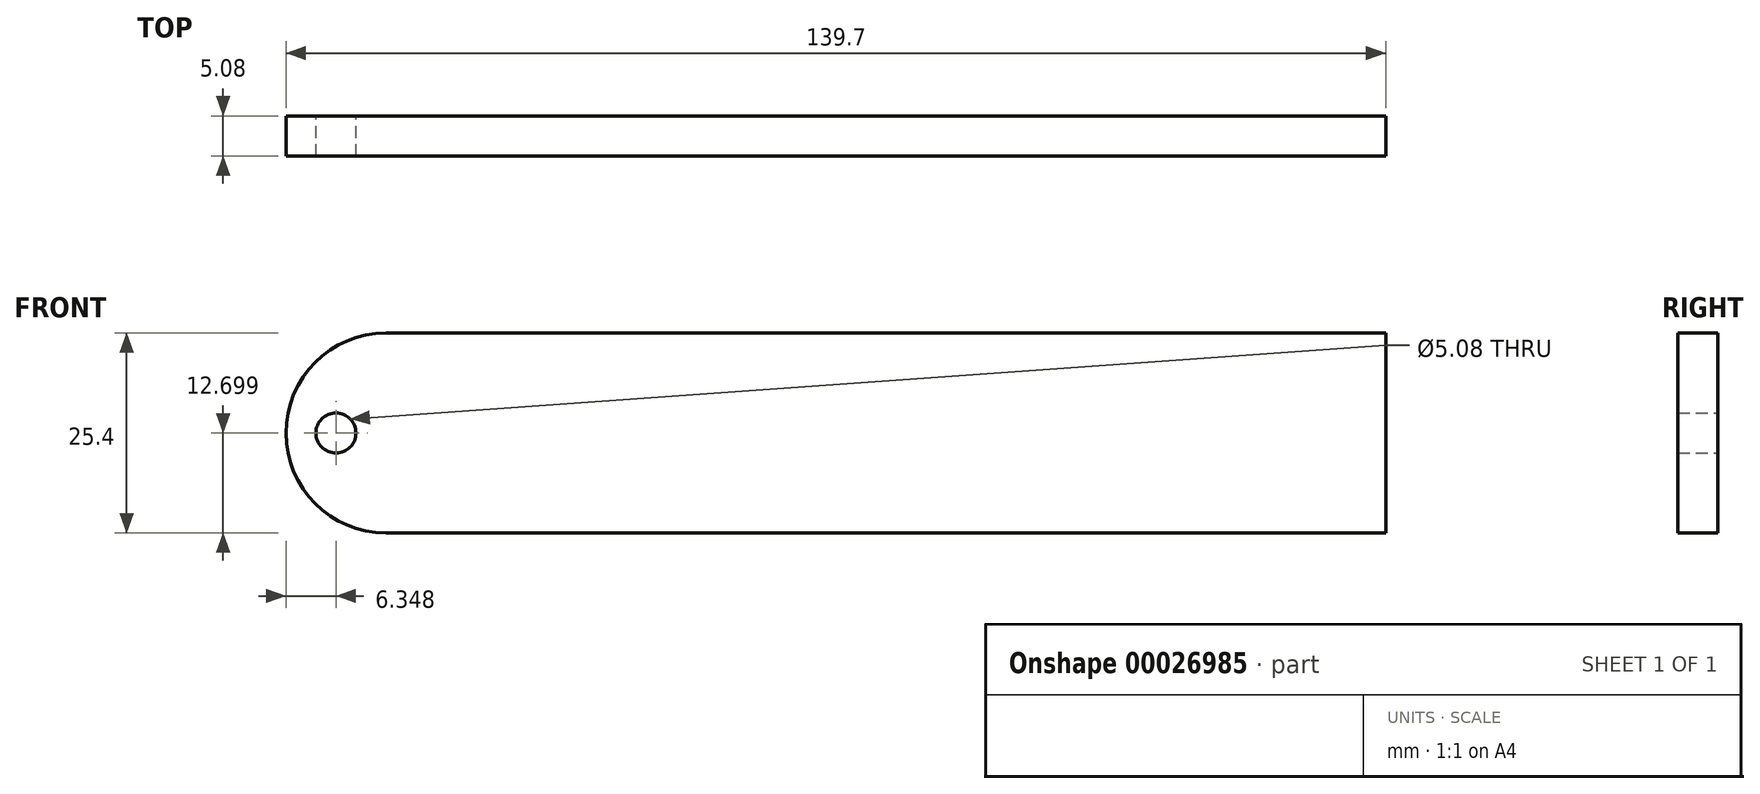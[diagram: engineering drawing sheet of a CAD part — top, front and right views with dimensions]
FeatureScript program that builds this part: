
annotation { "Feature Type Name" : "Feature", "Feature Type Description" : "" }
export const myFeature = defineFeature(function(context is Context, id is Id, definition is map)
    precondition{}
    {
        {
            var Q0;
            Q0=qCreatedBy(makeId("Front.planeOp"),FACE);
            var sketch = newSketch(context, id + "F0", { "sketchPlane" : qUnion([Q0])});
            skLineSegment(sketch, "E0.bottom", {"start": v(-67.9, 33.23) * mm, "end": v(59.1, 33.23) * mm});
            skLineSegment(sketch, "E0.top", {"start": v(-67.9, 7.83) * mm, "end": v(59.1, 7.83) * mm});
            skLineSegment(sketch, "E0.left", {"start": v(-67.9, 33.23) * mm, "end": v(-67.9, 7.83) * mm});
            skPoint(sketch, "E1", {"position": v(-67.9, 20.53) * mm});
            skArc(sketch, "E2", {"start": v(-67.9, 33.23) * mm, "mid": v(-80.6, 20.53) * mm, "end": v(-67.9, 7.83) * mm});
            skPoint(sketch, "E3", {"position": v(-74.24, 20.53) * mm});
            skPoint(sketch, "E4.orphan", {"position": v(-80.6, 20.53) * mm});
            skCircle(sketch, "E5", {"center": v(-74.24, 20.53) * mm, "radius": 2.54 * mm});
            skLineSegment(sketch, "E6", {"start": v(59.1, 33.23) * mm, "end": v(59.1, 7.83) * mm});
            skSolve(sketch);
        }
        {
            var Q0;
            Q0=makeQuery(id+"F0.imprint","IMPRINT",FACE,{"disambiguationData":[TD([[makeQuery(id+"F0.imprint","IMPRINT",EDGE,{"derivedFrom":sQuery(id+"F0.wireOp",EDGE,"E0.left")}),-1.0]])]});
            var Q1;
            Q1=makeQuery(id+"F0.imprint","IMPRINT",FACE,{"disambiguationData":[TD([[makeQuery(id+"F0.imprint","IMPRINT",EDGE,{"derivedFrom":sQuery(id+"F0.wireOp",EDGE,"E0.bottom")}),-1.0]])]});
            extrude(context, id + "F1", {"entities" : qUnion([Q0, Q1]), "depth" : 5.08 * mm});
        }
    });
